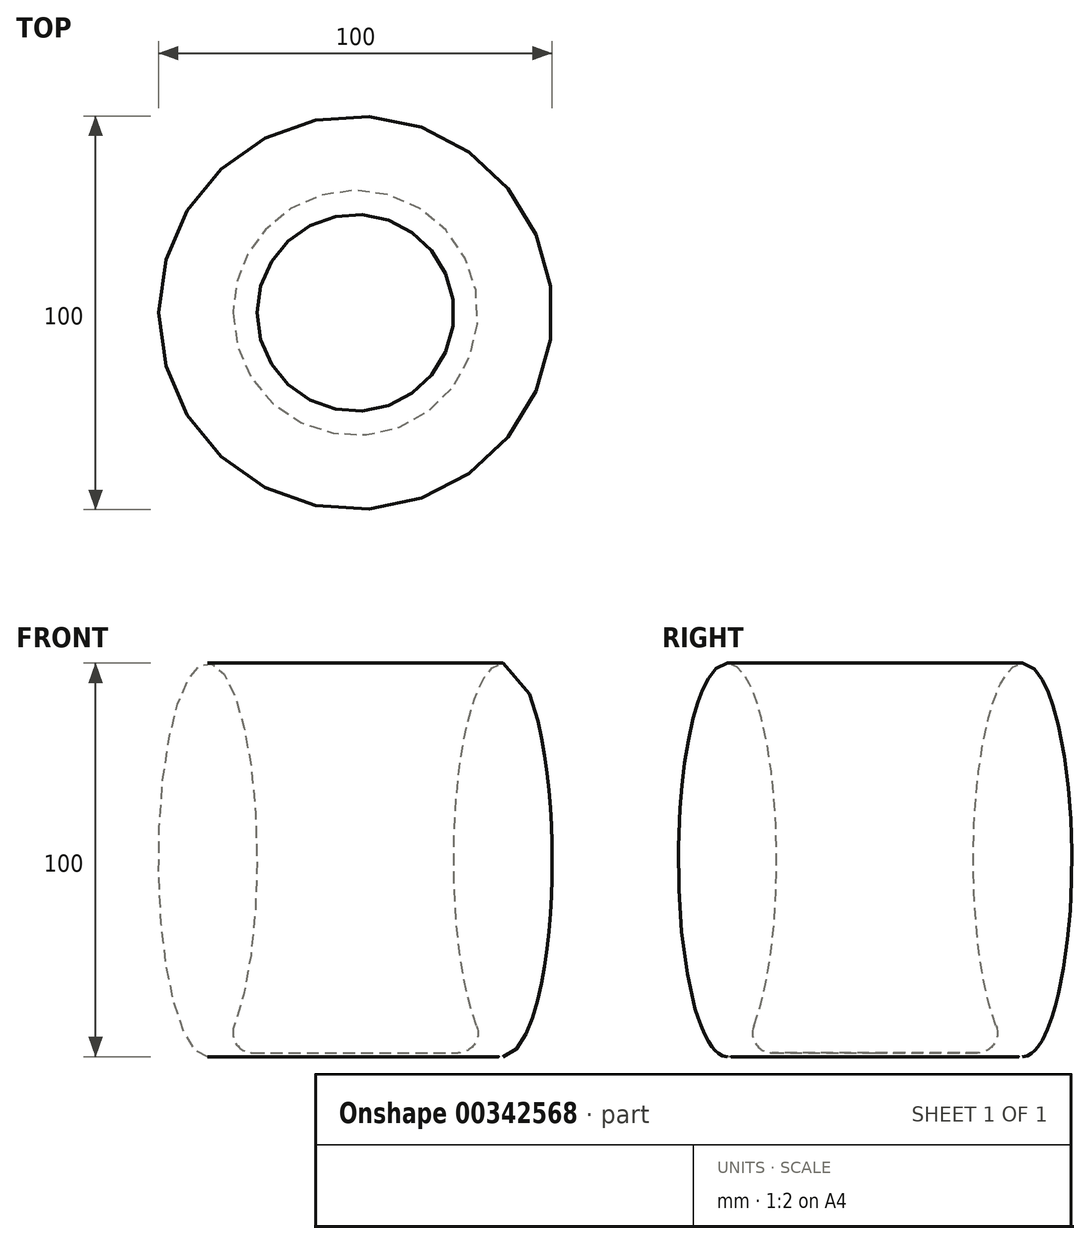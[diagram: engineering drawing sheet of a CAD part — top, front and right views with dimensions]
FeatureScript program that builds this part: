
annotation { "Feature Type Name" : "Feature", "Feature Type Description" : "" }
export const myFeature = defineFeature(function(context is Context, id is Id, definition is map)
    precondition{}
    {
        {
            var Q0;
            Q0=qCreatedBy(makeId("Front.planeOp"),FACE);
            var sketch = newSketch(context, id + "F0", { "sketchPlane" : qUnion([Q0])});
            skEllipticalArc(sketch, "E0", {});
            skLineSegment(sketch, "E1", {"start": v(0, 0) * mm, "end": v(0, 100) * mm, "construction": true});
            skPoint(sketch, "E2", {"position": v(25, 50) * mm});
            skPoint(sketch, "E3", {"position": v(50, 50) * mm});
            skLineSegment(sketch, "E4", {"start": v(37.5, 0) * mm, "end": v(0, 0) * mm});
            skLineSegment(sketch, "E5", {"start": v(0, 0) * mm, "end": v(0, 1) * mm});
            skLineSegment(sketch, "E6", {"start": v(0, 1) * mm, "end": v(26.13, 1) * mm});
            skPoint(sketch, "E7.orphan", {"position": v(37.5, 1) * mm});
            skPoint(sketch, "E8.visualSharp", {"position": v(35.01, 1) * mm});
            skArc(sketch, "E8.filletArc", {"start": v(26.13, 1) * mm, "mid": v(30.26, 3.18) * mm, "end": v(30.79, 7.83) * mm});
            const initialGuessF0  = {"E0": [0.0375, 0.05, 0, 1, 0.05, 0.0125, 3.141592653589793, 2.574489880964152]};
            skSetInitialGuess(sketch, initialGuessF0);
            skSolve(sketch);
        }
        {
            var Q0;
            Q0=makeQuery(id+"F0.imprint","IMPRINT",FACE,{"disambiguationData":[TD([[makeQuery(id+"F0.imprint","IMPRINT",EDGE,{"derivedFrom":sQuery(id+"F0.wireOp",EDGE,"E0")}),1.0]])]});
            var Q1;
            Q1=makeQuery(id+"F0.imprint","IMPRINT",FACE,{"disambiguationData":[TD([[makeQuery(id+"F0.imprint","IMPRINT",EDGE,{"derivedFrom":sQuery(id+"F0.wireOp",EDGE,"793c75fe-19e5-4459-9b79-2bd3d177ff24.0")}),1.0]])]});
            var Q2;
            Q2=sQuery(id+"F0.wireOp",EDGE,"E1");
            revolve(context, id + "F1", {"entities" : qUnion([Q0, Q1]), "axis" : qUnion([Q2]), "revolveType" : RevolveType.FULL});
        }
    });
